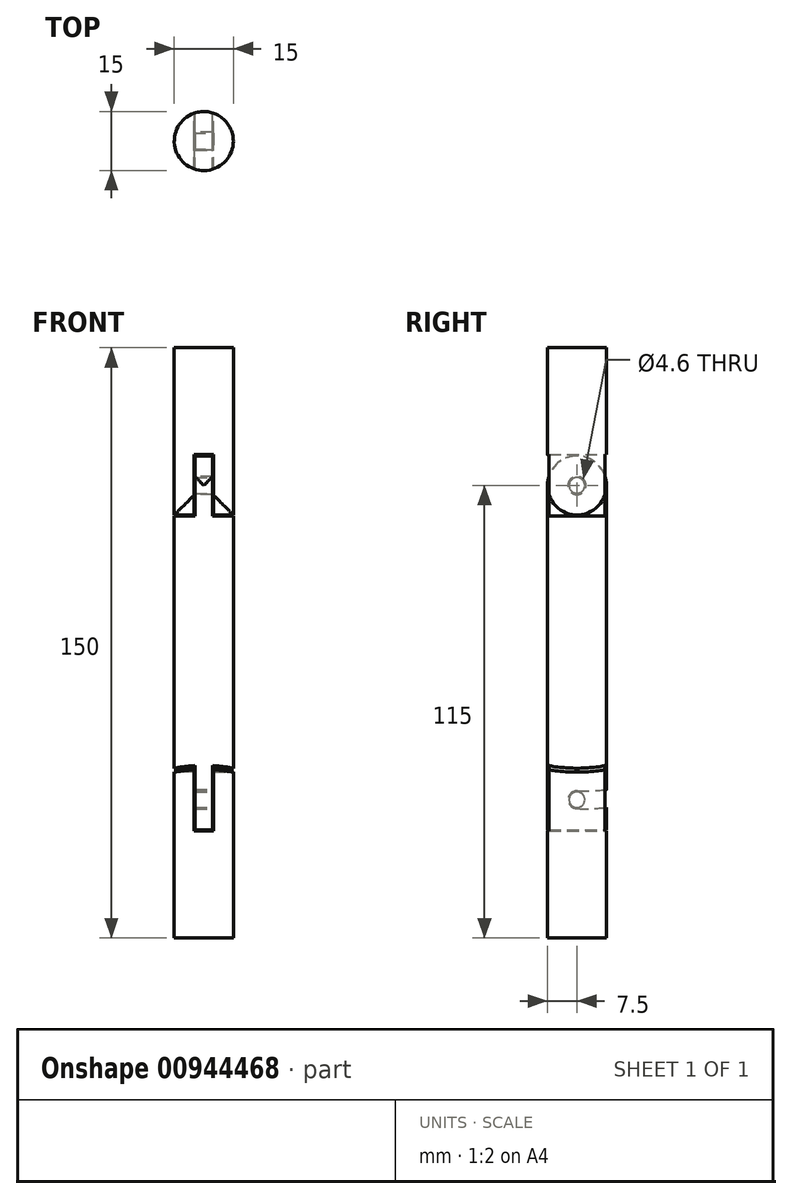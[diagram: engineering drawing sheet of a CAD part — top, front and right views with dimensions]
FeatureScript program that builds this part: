
annotation { "Feature Type Name" : "Feature", "Feature Type Description" : "" }
export const myFeature = defineFeature(function(context is Context, id is Id, definition is map)
    precondition{}
    {
        {
            var Q0;
            Q0=qCreatedBy(makeId("Top.planeOp"),FACE);
            var sketch = newSketch(context, id + "F0", { "sketchPlane" : qUnion([Q0])});
            skCircle(sketch, "E0", {"center": v(0, 0) * mm, "radius": 7.5 * mm});
            skSolve(sketch);
        }
        {
            var Q0;
            Q0 = qSketchRegion(id + "F0", true);
            extrude(context, id + "F1", {"entities" : qUnion([Q0]), "endBound" : BoundingType.SYMMETRIC, "depth" : 150 * mm, "offsetDistance" : 25 * mm});
        }
        {
            var Q0;
            Q0=qCreatedBy(makeId("Front.planeOp"),FACE);
            var sketch = newSketch(context, id + "F2", { "sketchPlane" : qUnion([Q0])});
            skLineSegment(sketch, "E1", {"start": v(0, 0) * mm, "end": v(0, 40) * mm});
            skLineSegment(sketch, "E2", {"start": v(0, 40) * mm, "end": v(2.2, 40) * mm});
            skLineSegment(sketch, "E3", {"start": v(2.2, 40) * mm, "end": v(2.2, 47.5) * mm});
            skLineSegment(sketch, "E4", {"start": v(2.2, 47.5) * mm, "end": v(0, 47.5) * mm});
            skLineSegment(sketch, "E5.MirrorCS", {"start": v(2.2, 40) * mm, "end": v(2.2, 32.5) * mm});
            skLineSegment(sketch, "E6.MirrorCS", {"start": v(2.2, 32.5) * mm, "end": v(0, 32.5) * mm});
            skLineSegment(sketch, "E7.MirrorCS", {"start": v(-2.2, 40) * mm, "end": v(-2.2, 47.5) * mm});
            skLineSegment(sketch, "E8.MirrorCS", {"start": v(-2.2, 47.5) * mm, "end": v(0, 47.5) * mm});
            skLineSegment(sketch, "E9.MirrorCS", {"start": v(-2.2, 32.5) * mm, "end": v(0, 32.5) * mm});
            skLineSegment(sketch, "E10.MirrorCS", {"start": v(-2.2, 40) * mm, "end": v(-2.2, 32.5) * mm});
            skLineSegment(sketch, "E11", {"start": v(0, 47.5) * mm, "end": v(0, 32.5) * mm});
            skLineSegment(sketch, "E12.0", {"start": v(2.5, 40) * mm, "end": v(2.5, 47.8) * mm});
            skLineSegment(sketch, "E12.1", {"start": v(2.5, 40) * mm, "end": v(2.5, 32.2) * mm});
            skLineSegment(sketch, "E12.2", {"start": v(2.5, 47.8) * mm, "end": v(0, 47.8) * mm});
            skLineSegment(sketch, "E12.3", {"start": v(2.5, 32.2) * mm, "end": v(0, 32.2) * mm});
            skLineSegment(sketch, "E12.4", {"start": v(-2.5, 47.8) * mm, "end": v(0, 47.8) * mm});
            skLineSegment(sketch, "E12.5", {"start": v(-2.5, 42.19) * mm, "end": v(-2.5, 47.8) * mm});
            skLineSegment(sketch, "E12.6", {"start": v(-2.5, 42.19) * mm, "end": v(-2.5, 32.2) * mm});
            skLineSegment(sketch, "E12.7", {"start": v(-2.5, 32.2) * mm, "end": v(0, 32.2) * mm});
            skLineSegment(sketch, "E13", {"start": v(2.2, 32.5) * mm, "end": v(2.2, 32.2) * mm});
            skPoint(sketch, "E13.endSnap0", {"position": v(1.25, 32.2) * mm});
            skLineSegment(sketch, "E14", {"start": v(-2.2, 32.5) * mm, "end": v(-2.2, 32.2) * mm});
            skLineSegment(sketch, "E15.MirrorCS", {"start": v(0, 0) * mm, "end": v(0, -40) * mm});
            skLineSegment(sketch, "E16.MirrorCS", {"start": v(2.5, -40) * mm, "end": v(2.5, -47.8) * mm});
            skLineSegment(sketch, "E17.MirrorCS", {"start": v(2.5, -47.8) * mm, "end": v(0, -47.8) * mm});
            skLineSegment(sketch, "E18.MirrorCS", {"start": v(-2.5, -47.8) * mm, "end": v(0, -47.8) * mm});
            skLineSegment(sketch, "E19.MirrorCS", {"start": v(-2.5, -42.19) * mm, "end": v(-2.5, -47.8) * mm});
            skLineSegment(sketch, "E20.MirrorCS", {"start": v(-2.2, -40) * mm, "end": v(-2.2, -47.5) * mm});
            skLineSegment(sketch, "E21.MirrorCS", {"start": v(-2.2, -47.5) * mm, "end": v(0, -47.5) * mm});
            skLineSegment(sketch, "E22.MirrorCS", {"start": v(2.2, -47.5) * mm, "end": v(0, -47.5) * mm});
            skLineSegment(sketch, "E23.MirrorCS", {"start": v(2.2, -40) * mm, "end": v(2.2, -47.5) * mm});
            skLineSegment(sketch, "E24.MirrorCS", {"start": v(-2.5, -42.19) * mm, "end": v(-2.5, -32.2) * mm});
            skLineSegment(sketch, "E25.MirrorCS", {"start": v(-2.2, -40) * mm, "end": v(-2.2, -32.5) * mm});
            skLineSegment(sketch, "E26.MirrorCS", {"start": v(2.2, -40) * mm, "end": v(2.2, -32.5) * mm});
            skLineSegment(sketch, "E27.MirrorCS", {"start": v(2.5, -40) * mm, "end": v(2.5, -32.2) * mm});
            skLineSegment(sketch, "E28.MirrorCS", {"start": v(2.5, -32.2) * mm, "end": v(0, -32.2) * mm});
            skLineSegment(sketch, "E29.MirrorCS", {"start": v(2.2, -32.5) * mm, "end": v(0, -32.5) * mm});
            skLineSegment(sketch, "E30.MirrorCS", {"start": v(-2.2, -32.5) * mm, "end": v(0, -32.5) * mm});
            skLineSegment(sketch, "E31.MirrorCS", {"start": v(-2.5, -32.2) * mm, "end": v(0, -32.2) * mm});
            skLineSegment(sketch, "E32.MirrorCS", {"start": v(2.2, -32.5) * mm, "end": v(2.2, -32.2) * mm});
            skLineSegment(sketch, "E33.MirrorCS", {"start": v(-2.2, -32.5) * mm, "end": v(-2.2, -32.2) * mm});
            skSolve(sketch);
        }
        {
            var Q0;
            Q0=makeQuery(id+"F2.imprint","IMPRINT",FACE,{"disambiguationData":[TD([[makeQuery(id+"F2.imprint","IMPRINT",EDGE,{"derivedFrom":sQuery(id+"F2.wireOp",EDGE,"E3")}),-1.0]])]});
            extrude(context, id + "F3", {"entities" : qUnion([Q0]), "operationType" : NewBodyOperationType.REMOVE, "endBound" : BoundingType.SYMMETRIC, "depth" : 25 * mm, "offsetDistance" : 25 * mm});
        }
        {
            var Q0;
            Q0=makeQuery(id+"F3.boolean.opBoolean","COPY",FACE,{"derivedFrom":makeQuery(id+"F3.opExtrude","SWEPT_FACE",FACE,{"disambiguationData":[OSD([sQuery(id+"F2.wireOp",EDGE,"E3"),sQuery(id+"F2.wireOp",EDGE,"E5.MirrorCS"),sQuery(id+"F2.wireOp",EDGE,"E13")])]})});
            cPlane(context, id + "F4", {"entities" : qUnion([Q0]), "cplaneType" : CPlaneType.OFFSET, "offset" : .15 * mm, "width" : 150 * mm, "height" : 150 * mm});
        }
        {
            var Q0;
            Q0=qCreatedBy(id+"F4.planeOp",FACE);
            var sketch = newSketch(context, id + "F5", { "sketchPlane" : qUnion([Q0])});
            skLineSegment(sketch, "E34", {"start": v(0, 0) * mm, "end": v(0, 40) * mm});
            skCircle(sketch, "E35", {"center": v(0, 40) * mm, "radius": 2 * mm});
            skCircle(sketch, "E36", {"center": v(0, 40) * mm, "radius": 2.3 * mm});
            skCircle(sketch, "E37", {"center": v(0, 40) * mm, "radius": 7.8 * mm});
            skCircle(sketch, "E38", {"center": v(0, 40) * mm, "radius": 7.5 * mm});
            skLineSegment(sketch, "E39", {"start": v(0, 40) * mm, "end": v(-7.5, 40) * mm});
            skLineSegment(sketch, "E40", {"start": v(-7.5, 40) * mm, "end": v(7.8, 40) * mm});
            skLineSegment(sketch, "E41", {"start": v(7.8, 40) * mm, "end": v(7.8, 47.8) * mm});
            skLineSegment(sketch, "E42", {"start": v(7.8, 47.8) * mm, "end": v(0, 47.8) * mm});
            skLineSegment(sketch, "E43.MirrorCS", {"start": v(-7.8, 47.8) * mm, "end": v(0, 47.8) * mm});
            skLineSegment(sketch, "E44.MirrorCS", {"start": v(-7.8, 40) * mm, "end": v(-7.8, 47.8) * mm});
            skLineSegment(sketch, "E45.MirrorCS", {"start": v(7.8, 40) * mm, "end": v(7.8, 32.2) * mm});
            skLineSegment(sketch, "E46.MirrorCS", {"start": v(7.8, 32.2) * mm, "end": v(0, 32.2) * mm});
            skLineSegment(sketch, "E47.MirrorCS", {"start": v(-7.8, 32.2) * mm, "end": v(0, 32.2) * mm});
            skLineSegment(sketch, "E48.MirrorCS", {"start": v(-7.8, 40) * mm, "end": v(-7.8, 32.2) * mm});
            skLineSegment(sketch, "E49", {"start": v(-7.5, 40) * mm, "end": v(-7.8, 40) * mm});
            skSolve(sketch);
        }
        {
            var Q0;
            Q0=makeQuery(id+"F3.boolean.opBoolean","COPY",FACE,{"derivedFrom":makeQuery(id+"F3.opExtrude","SWEPT_FACE",FACE,{"disambiguationData":[OSD([sQuery(id+"F2.wireOp",EDGE,"E7.MirrorCS"),sQuery(id+"F2.wireOp",EDGE,"E10.MirrorCS"),sQuery(id+"F2.wireOp",EDGE,"E14")])]})});
            cPlane(context, id + "F6", {"entities" : qUnion([Q0]), "cplaneType" : CPlaneType.OFFSET, "offset" : .15 * mm, "width" : 150 * mm, "height" : 150 * mm});
        }
        {
            var Q0;
            Q0=qCreatedBy(id+"F6.planeOp",FACE);
            var sketch = newSketch(context, id + "F7", { "sketchPlane" : qUnion([Q0])});
            skLineSegment(sketch, "E50", {"start": v(0, 0) * mm, "end": v(0, 40) * mm});
            skCircle(sketch, "E51", {"center": v(0, 40) * mm, "radius": 2 * mm});
            skCircle(sketch, "E52", {"center": v(0, 40) * mm, "radius": 2.3 * mm});
            skCircle(sketch, "E53", {"center": v(0, 40) * mm, "radius": 7.8 * mm});
            skCircle(sketch, "E54", {"center": v(0, 40) * mm, "radius": 7.5 * mm});
            skLineSegment(sketch, "E55", {"start": v(0, 40) * mm, "end": v(-7.5, 40) * mm});
            skLineSegment(sketch, "E56", {"start": v(-7.5, 40) * mm, "end": v(7.8, 40) * mm});
            skLineSegment(sketch, "E57", {"start": v(7.8, 40) * mm, "end": v(7.8, 47.8) * mm});
            skLineSegment(sketch, "E58", {"start": v(7.8, 47.8) * mm, "end": v(0, 47.8) * mm});
            skLineSegment(sketch, "E59.MirrorCS", {"start": v(-7.8, 47.8) * mm, "end": v(0, 47.8) * mm});
            skLineSegment(sketch, "E60.MirrorCS", {"start": v(-7.8, 40) * mm, "end": v(-7.8, 47.8) * mm});
            skLineSegment(sketch, "E61.MirrorCS", {"start": v(7.8, 40) * mm, "end": v(7.8, 32.2) * mm});
            skLineSegment(sketch, "E62.MirrorCS", {"start": v(7.8, 32.2) * mm, "end": v(0, 32.2) * mm});
            skLineSegment(sketch, "E63.MirrorCS", {"start": v(-7.8, 32.2) * mm, "end": v(0, 32.2) * mm});
            skLineSegment(sketch, "E64.MirrorCS", {"start": v(-7.8, 40) * mm, "end": v(-7.8, 32.2) * mm});
            skLineSegment(sketch, "E65", {"start": v(-7.5, 40) * mm, "end": v(-7.8, 40) * mm});
            skSolve(sketch);
        }
        {
            var Q0;
            {var subQ0=sQuery(id+"F7.wireOp",EDGE,"E55");var subQ1=sQuery(id+"F7.wireOp",EDGE,"E51");var subQ2=makeQuery(id+"F7.imprint","INTERSECT",VERTEX,{"derivedFrom":[subQ1,subQ0]});Q0=makeQuery(id+"F7.imprint","IMPRINT",FACE,{"disambiguationData":[TD([[makeQuery(id+"F7.imprint","IMPRINT",EDGE,{"disambiguationData":[TD([[subQ2,1.0]])],"derivedFrom":subQ1}),1.0]])]});}
            var Q1;
            {var subQ1=sQuery(id+"F7.wireOp",EDGE,"E50");var subQ3=sQuery(id+"F7.wireOp",EDGE,"E51");var subQ4=makeQuery(id+"F7.imprint","INTERSECT",VERTEX,{"derivedFrom":[subQ1,subQ3]});Q1=makeQuery(id+"F7.imprint","IMPRINT",FACE,{"disambiguationData":[TD([[makeQuery(id+"F7.imprint","IMPRINT",EDGE,{"disambiguationData":[TD([[subQ4,-1.0]])],"derivedFrom":subQ3}),1.0]])]});}
            var Q2;
            {var subQ0=sQuery(id+"F7.wireOp",EDGE,"E52");var subQ1=sQuery(id+"F7.wireOp",EDGE,"E50");var subQ2=makeQuery(id+"F7.imprint","INTERSECT",VERTEX,{"derivedFrom":[subQ1,subQ0]});Q2=makeQuery(id+"F7.imprint","IMPRINT",FACE,{"disambiguationData":[TD([[makeQuery(id+"F7.imprint","IMPRINT",EDGE,{"disambiguationData":[TD([[subQ2,-1.0]])],"derivedFrom":subQ1}),-1.0]])]});}
            var Q3;
            {var subQ1=sQuery(id+"F7.wireOp",EDGE,"E50");var subQ3=sQuery(id+"F7.wireOp",EDGE,"E51");var subQ4=makeQuery(id+"F7.imprint","INTERSECT",VERTEX,{"derivedFrom":[subQ1,subQ3]});Q3=makeQuery(id+"F7.imprint","IMPRINT",FACE,{"disambiguationData":[TD([[makeQuery(id+"F7.imprint","IMPRINT",EDGE,{"disambiguationData":[TD([[subQ4,1.0]])],"derivedFrom":subQ3}),1.0]])]});}
            var Q4;
            {var subQ0=sQuery(id+"F7.wireOp",EDGE,"E52");var subQ1=sQuery(id+"F7.wireOp",EDGE,"E50");var subQ2=makeQuery(id+"F7.imprint","INTERSECT",VERTEX,{"derivedFrom":[subQ1,subQ0]});Q4=makeQuery(id+"F7.imprint","IMPRINT",FACE,{"disambiguationData":[TD([[makeQuery(id+"F7.imprint","IMPRINT",EDGE,{"disambiguationData":[TD([[subQ2,-1.0]])],"derivedFrom":subQ1}),1.0]])]});}
            var Q5;
            {var subQ0=sQuery(id+"F7.wireOp",EDGE,"E55");var subQ1=sQuery(id+"F7.wireOp",EDGE,"E51");var subQ2=makeQuery(id+"F7.imprint","INTERSECT",VERTEX,{"derivedFrom":[subQ1,subQ0]});Q5=makeQuery(id+"F7.imprint","IMPRINT",FACE,{"disambiguationData":[TD([[makeQuery(id+"F7.imprint","IMPRINT",EDGE,{"disambiguationData":[TD([[subQ2,1.0]])],"derivedFrom":subQ1}),-1.0]])]});}
            extrude(context, id + "F8", {"entities" : qUnion([Q0, Q1, Q2, Q3, Q4, Q5]), "operationType" : NewBodyOperationType.REMOVE, "oppositeDirection" : true, "depth" : 4.8 * mm, "offsetDistance" : 25 * mm});
        }
        {
            var Q0;
            {var subQ2=sQuery(id+"F5.wireOp",EDGE,"E47.MirrorCS");Q0=makeQuery(id+"F5.imprint","IMPRINT",FACE,{"disambiguationData":[TD([[makeQuery(id+"F5.imprint","IMPRINT",EDGE,{"derivedFrom":subQ2}),1.0]])]});}
            var Q1;
            {var subQ5=sQuery(id+"F5.wireOp",EDGE,"E49");Q1=makeQuery(id+"F5.imprint","IMPRINT",FACE,{"disambiguationData":[TD([[makeQuery(id+"F5.imprint","IMPRINT",EDGE,{"derivedFrom":subQ5}),1.0]])]});}
            var Q2;
            {var subQ0=sQuery(id+"F5.wireOp",EDGE,"E38");var subQ1=sQuery(id+"F5.wireOp",EDGE,"E34");var subQ2=makeQuery(id+"F5.imprint","INTERSECT",VERTEX,{"derivedFrom":[subQ1,subQ0]});Q2=makeQuery(id+"F5.imprint","IMPRINT",FACE,{"disambiguationData":[TD([[makeQuery(id+"F5.imprint","IMPRINT",EDGE,{"disambiguationData":[TD([[subQ2,-1.0]])],"derivedFrom":subQ0}),-1.0]])]});}
            var Q3;
            {var subQ0=sQuery(id+"F5.wireOp",EDGE,"E45.MirrorCS");Q3=makeQuery(id+"F5.imprint","IMPRINT",FACE,{"disambiguationData":[TD([[makeQuery(id+"F5.imprint","IMPRINT",EDGE,{"derivedFrom":subQ0}),-1.0]])]});}
            extrude(context, id + "F9", {"entities" : qUnion([Q0, Q1, Q2, Q3]), "operationType" : NewBodyOperationType.REMOVE, "depth" : 25 * mm, "offsetDistance" : 25 * mm});
        }
        {
            var Q0;
            {var subQ0=sQuery(id+"F5.wireOp",EDGE,"E41");Q0=makeQuery(id+"F5.imprint","IMPRINT",FACE,{"disambiguationData":[TD([[makeQuery(id+"F5.imprint","IMPRINT",EDGE,{"derivedFrom":subQ0}),1.0]])]});}
            var Q1;
            {var subQ0=sQuery(id+"F5.wireOp",EDGE,"E49");Q1=makeQuery(id+"F5.imprint","IMPRINT",FACE,{"disambiguationData":[TD([[makeQuery(id+"F5.imprint","IMPRINT",EDGE,{"derivedFrom":subQ0}),-1.0]])]});}
            var Q2;
            {var subQ0=sQuery(id+"F5.wireOp",EDGE,"E43.MirrorCS");Q2=makeQuery(id+"F5.imprint","IMPRINT",FACE,{"disambiguationData":[TD([[makeQuery(id+"F5.imprint","IMPRINT",EDGE,{"derivedFrom":subQ0}),-1.0]])]});}
            extrude(context, id + "F10", {"entities" : qUnion([Q0, Q1, Q2]), "operationType" : NewBodyOperationType.REMOVE, "oppositeDirection" : true, "depth" : 4.6 * mm, "offsetDistance" : 25 * mm});
        }
        {
            var Q0;
            {var subQ0=sQuery(id+"F7.wireOp",EDGE,"E61.MirrorCS");Q0=makeQuery(id+"F7.imprint","IMPRINT",FACE,{"disambiguationData":[TD([[makeQuery(id+"F7.imprint","IMPRINT",EDGE,{"derivedFrom":subQ0}),-1.0]])]});}
            var Q1;
            {var subQ0=sQuery(id+"F7.wireOp",EDGE,"E54");var subQ1=sQuery(id+"F7.wireOp",EDGE,"E50");var subQ2=makeQuery(id+"F7.imprint","INTERSECT",VERTEX,{"derivedFrom":[subQ1,subQ0]});Q1=makeQuery(id+"F7.imprint","IMPRINT",FACE,{"disambiguationData":[TD([[makeQuery(id+"F7.imprint","IMPRINT",EDGE,{"disambiguationData":[TD([[subQ2,-1.0]])],"derivedFrom":subQ0}),-1.0]])]});}
            var Q2;
            {var subQ5=sQuery(id+"F7.wireOp",EDGE,"E65");Q2=makeQuery(id+"F7.imprint","IMPRINT",FACE,{"disambiguationData":[TD([[makeQuery(id+"F7.imprint","IMPRINT",EDGE,{"derivedFrom":subQ5}),1.0]])]});}
            var Q3;
            {var subQ2=sQuery(id+"F7.wireOp",EDGE,"E63.MirrorCS");Q3=makeQuery(id+"F7.imprint","IMPRINT",FACE,{"disambiguationData":[TD([[makeQuery(id+"F7.imprint","IMPRINT",EDGE,{"derivedFrom":subQ2}),1.0]])]});}
            extrude(context, id + "F11", {"entities" : qUnion([Q0, Q1, Q2, Q3]), "operationType" : NewBodyOperationType.REMOVE, "depth" : 25 * mm, "offsetDistance" : 25 * mm});
        }
        {
            var Q0;
            {var subQ0=sQuery(id+"F7.wireOp",EDGE,"E55");var subQ1=sQuery(id+"F7.wireOp",EDGE,"E51");var subQ2=makeQuery(id+"F7.imprint","INTERSECT",VERTEX,{"derivedFrom":[subQ1,subQ0]});Q0=makeQuery(id+"F7.imprint","IMPRINT",FACE,{"disambiguationData":[TD([[makeQuery(id+"F7.imprint","IMPRINT",EDGE,{"disambiguationData":[TD([[subQ2,1.0]])],"derivedFrom":subQ1}),1.0]])]});}
            var Q1;
            {var subQ1=sQuery(id+"F7.wireOp",EDGE,"E50");var subQ3=sQuery(id+"F7.wireOp",EDGE,"E51");var subQ4=makeQuery(id+"F7.imprint","INTERSECT",VERTEX,{"derivedFrom":[subQ1,subQ3]});Q1=makeQuery(id+"F7.imprint","IMPRINT",FACE,{"disambiguationData":[TD([[makeQuery(id+"F7.imprint","IMPRINT",EDGE,{"disambiguationData":[TD([[subQ4,1.0]])],"derivedFrom":subQ3}),1.0]])]});}
            var Q2;
            {var subQ0=sQuery(id+"F7.wireOp",EDGE,"E52");var subQ1=sQuery(id+"F7.wireOp",EDGE,"E50");var subQ2=makeQuery(id+"F7.imprint","INTERSECT",VERTEX,{"derivedFrom":[subQ1,subQ0]});Q2=makeQuery(id+"F7.imprint","IMPRINT",FACE,{"disambiguationData":[TD([[makeQuery(id+"F7.imprint","IMPRINT",EDGE,{"disambiguationData":[TD([[subQ2,-1.0]])],"derivedFrom":subQ1}),-1.0]])]});}
            var Q3;
            {var subQ1=sQuery(id+"F7.wireOp",EDGE,"E50");var subQ3=sQuery(id+"F7.wireOp",EDGE,"E51");var subQ4=makeQuery(id+"F7.imprint","INTERSECT",VERTEX,{"derivedFrom":[subQ1,subQ3]});Q3=makeQuery(id+"F7.imprint","IMPRINT",FACE,{"disambiguationData":[TD([[makeQuery(id+"F7.imprint","IMPRINT",EDGE,{"disambiguationData":[TD([[subQ4,-1.0]])],"derivedFrom":subQ3}),1.0]])]});}
            var Q4;
            {var subQ0=sQuery(id+"F7.wireOp",EDGE,"E55");var subQ1=sQuery(id+"F7.wireOp",EDGE,"E51");var subQ2=makeQuery(id+"F7.imprint","INTERSECT",VERTEX,{"derivedFrom":[subQ1,subQ0]});Q4=makeQuery(id+"F7.imprint","IMPRINT",FACE,{"disambiguationData":[TD([[makeQuery(id+"F7.imprint","IMPRINT",EDGE,{"disambiguationData":[TD([[subQ2,1.0]])],"derivedFrom":subQ1}),-1.0]])]});}
            var Q5;
            {var subQ0=sQuery(id+"F7.wireOp",EDGE,"E52");var subQ1=sQuery(id+"F7.wireOp",EDGE,"E50");var subQ2=makeQuery(id+"F7.imprint","INTERSECT",VERTEX,{"derivedFrom":[subQ1,subQ0]});Q5=makeQuery(id+"F7.imprint","IMPRINT",FACE,{"disambiguationData":[TD([[makeQuery(id+"F7.imprint","IMPRINT",EDGE,{"disambiguationData":[TD([[subQ2,-1.0]])],"derivedFrom":subQ1}),1.0]])]});}
            extrude(context, id + "F12", {"entities" : qUnion([Q0, Q1, Q2, Q3, Q4, Q5]), "operationType" : NewBodyOperationType.REMOVE, "oppositeDirection" : true, "depth" : 4.7 * mm, "offsetDistance" : 25 * mm});
        }
        {
            var Q0;
            {var subQ0=sQuery(id+"F7.wireOp",EDGE,"E55");var subQ1=sQuery(id+"F7.wireOp",EDGE,"E51");var subQ2=makeQuery(id+"F7.imprint","INTERSECT",VERTEX,{"derivedFrom":[subQ1,subQ0]});Q0=makeQuery(id+"F7.imprint","IMPRINT",FACE,{"disambiguationData":[TD([[makeQuery(id+"F7.imprint","IMPRINT",EDGE,{"disambiguationData":[TD([[subQ2,1.0]])],"derivedFrom":subQ1}),1.0]])]});}
            var Q1;
            {var subQ1=sQuery(id+"F7.wireOp",EDGE,"E50");var subQ3=sQuery(id+"F7.wireOp",EDGE,"E51");var subQ4=makeQuery(id+"F7.imprint","INTERSECT",VERTEX,{"derivedFrom":[subQ1,subQ3]});Q1=makeQuery(id+"F7.imprint","IMPRINT",FACE,{"disambiguationData":[TD([[makeQuery(id+"F7.imprint","IMPRINT",EDGE,{"disambiguationData":[TD([[subQ4,1.0]])],"derivedFrom":subQ3}),1.0]])]});}
            var Q2;
            {var subQ1=sQuery(id+"F7.wireOp",EDGE,"E50");var subQ3=sQuery(id+"F7.wireOp",EDGE,"E51");var subQ4=makeQuery(id+"F7.imprint","INTERSECT",VERTEX,{"derivedFrom":[subQ1,subQ3]});Q2=makeQuery(id+"F7.imprint","IMPRINT",FACE,{"disambiguationData":[TD([[makeQuery(id+"F7.imprint","IMPRINT",EDGE,{"disambiguationData":[TD([[subQ4,-1.0]])],"derivedFrom":subQ3}),1.0]])]});}
            extrude(context, id + "F13", {"entities" : qUnion([Q0, Q1, Q2]), "operationType" : NewBodyOperationType.ADD, "depth" : 3 * mm, "offsetDistance" : 25 * mm, "hasSecondDirection" : true, "secondDirectionOppositeDirection" : true, "secondDirectionDepth" : 6 * mm});
        }
        {
            var Q0;
            Q0=makeQuery(id+"F2.imprint","IMPRINT",FACE,{"disambiguationData":[TD([[makeQuery(id+"F2.imprint","IMPRINT",EDGE,{"derivedFrom":sQuery(id+"F2.wireOp",EDGE,"E16.MirrorCS")}),-1.0]])]});
            extrude(context, id + "F14", {"entities" : qUnion([Q0]), "operationType" : NewBodyOperationType.REMOVE, "endBound" : BoundingType.SYMMETRIC, "depth" : 25 * mm, "offsetDistance" : 25 * mm});
        }
        {
            var Q0;
            Q0=makeQuery(id+"F14.boolean.opBoolean","COPY",FACE,{"derivedFrom":makeQuery(id+"F14.opExtrude","SWEPT_FACE",FACE,{"disambiguationData":[OSD([sQuery(id+"F2.wireOp",EDGE,"E23.MirrorCS"),sQuery(id+"F2.wireOp",EDGE,"E26.MirrorCS"),sQuery(id+"F2.wireOp",EDGE,"E32.MirrorCS")])]})});
            var sketch = newSketch(context, id + "F15", { "sketchPlane" : qUnion([Q0])});
            skLineSegment(sketch, "E66", {"start": v(-7.17, -32.2) * mm, "end": v(0, -39.85) * mm});
            skLineSegment(sketch, "E67", {"start": v(7.17, -32.2) * mm, "end": v(0, -39.85) * mm});
            skLineSegment(sketch, "E68", {"start": v(0, -39.85) * mm, "end": v(7.17, -47.5) * mm});
            skLineSegment(sketch, "E69", {"start": v(0, -39.85) * mm, "end": v(-7.17, -47.5) * mm});
            skArc(sketch, "E70", {"start": v(0, -39.85) * mm, "mid": v(6.9, -39.59) * mm, "end": v(13.66, -38.14) * mm});
            skArc(sketch, "E71.0.startCap", {"start": v(-0.11, -42.1) * mm, "mid": v(-2.25, -39.74) * mm, "end": v(0.11, -37.6) * mm});
            skArc(sketch, "E71.0.endCap", {"start": v(13, -35.99) * mm, "mid": v(15.81, -37.48) * mm, "end": v(14.32, -40.29) * mm});
            skArc(sketch, "E71.0.left", {"start": v(0.11, -37.6) * mm, "mid": v(6.63, -37.36) * mm, "end": v(13, -35.99) * mm});
            skArc(sketch, "E71.0.right", {"start": v(-0.11, -42.1) * mm, "mid": v(7.19, -41.82) * mm, "end": v(14.32, -40.29) * mm});
            skCircle(sketch, "E72", {"center": v(0, -39.85) * mm, "radius": 2 * mm});
            skSolve(sketch);
        }
        {
            var Q0;
            Q0 = qSketchRegion(id + "F15", true);
            extrude(context, id + "F16", {"entities" : qUnion([Q0]), "operationType" : NewBodyOperationType.REMOVE, "oppositeDirection" : true, "depth" : 4.6 * mm, "offsetDistance" : 25 * mm});
        }
        {
            var Q0;
            Q0=qCreatedBy(makeId("Right.planeOp"),FACE);
            cPlane(context, id + "F17", {"entities" : qUnion([Q0]), "cplaneType" : CPlaneType.OFFSET, "offset" : 10 * mm, "oppositeDirection" : true, "width" : 150 * mm, "height" : 150 * mm});
        }
        {
            var Q0;
            Q0=qCreatedBy(makeId("Right.planeOp"),FACE);
            cPlane(context, id + "F18", {"entities" : qUnion([Q0]), "cplaneType" : CPlaneType.OFFSET, "offset" : 10 * mm, "width" : 150 * mm, "height" : 150 * mm});
        }
        {
            var Q0;
            Q0=qCreatedBy(id+"F18.planeOp",FACE);
            var sketch = newSketch(context, id + "F19", { "sketchPlane" : qUnion([Q0])});
            skCircle(sketch, "E73", {"center": v(0, 8) * mm, "radius": 39.85 * mm});
            skCircle(sketch, "E74", {"center": v(0, 8) * mm, "radius": 40.85 * mm});
            skLineSegment(sketch, "E75", {"start": v(0, -32.84) * mm, "end": v(9.2, -32.84) * mm});
            skPoint(sketch, "E76.start.orphan", {"position": v(0, -31.84) * mm});
            skLineSegment(sketch, "E77", {"start": v(10.2, -30.52) * mm, "end": v(10.2, -31.55) * mm});
            skLineSegment(sketch, "E78", {"start": v(-10.4, -30.46) * mm, "end": v(-10.4, -31.5) * mm});
            skLineSegment(sketch, "E79", {"start": v(0, 8) * mm, "end": v(0, 0) * mm});
            skSolve(sketch);
        }
        {
            var Q0;
            {var subQ2=sQuery(id+"F19.wireOp",EDGE,"E77");Q0=makeQuery(id+"F19.imprint","IMPRINT",FACE,{"disambiguationData":[TD([[makeQuery(id+"F19.imprint","IMPRINT",EDGE,{"derivedFrom":subQ2}),-1.0]])]});}
            extrude(context, id + "F20", {"entities" : qUnion([Q0]), "operationType" : NewBodyOperationType.REMOVE, "oppositeDirection" : true, "depth" : 7.8 * mm, "offsetDistance" : 25 * mm});
        }
        {
            var Q0;
            Q0=qCreatedBy(id+"F17.planeOp",FACE);
            cPlane(context, id + "F21", {"entities" : qUnion([Q0]), "cplaneType" : CPlaneType.OFFSET, "offset" : 6 * mm, "oppositeDirection" : true, "width" : 150 * mm, "height" : 150 * mm});
        }
        {
            var Q0;
            Q0=qCreatedBy(id+"F21.planeOp",FACE);
            var sketch = newSketch(context, id + "F22", { "sketchPlane" : qUnion([Q0])});
            skCircle(sketch, "E80", {"center": v(0, 8) * mm, "radius": 39.85 * mm});
            skCircle(sketch, "E81", {"center": v(0, 8) * mm, "radius": 40.85 * mm});
            skLineSegment(sketch, "E82", {"start": v(0, -32.84) * mm, "end": v(9.2, -32.84) * mm});
            skPoint(sketch, "E83.start.orphan", {"position": v(0, -31.84) * mm});
            skLineSegment(sketch, "E84", {"start": v(10.2, -30.52) * mm, "end": v(10.2, -31.55) * mm});
            skLineSegment(sketch, "E85", {"start": v(-10.4, -30.46) * mm, "end": v(-10.4, -31.5) * mm});
            skLineSegment(sketch, "E86", {"start": v(0, 8) * mm, "end": v(0, 0) * mm});
            skSolve(sketch);
        }
        {
            var Q0;
            {var subQ2=sQuery(id+"F22.wireOp",EDGE,"E84");Q0=makeQuery(id+"F22.imprint","IMPRINT",FACE,{"disambiguationData":[TD([[makeQuery(id+"F22.imprint","IMPRINT",EDGE,{"derivedFrom":subQ2}),-1.0]])]});}
            extrude(context, id + "F23", {"entities" : qUnion([Q0]), "operationType" : NewBodyOperationType.REMOVE, "depth" : 13.8 * mm, "offsetDistance" : 25 * mm});
        }
        {
            var Q0;
            Q0=makeQuery(id+"F16.boolean.opBoolean","SPLIT",FACE,{"disambiguationData":[TD([makeQuery(id+"F16.opExtrude","SWEPT_FACE",FACE,{"disambiguationData":[OSD([sQuery(id+"F15.wireOp",EDGE,"E72")])]})])],"derivedFrom":makeQuery(id+"F14.boolean.opBoolean","COPY",FACE,{"derivedFrom":makeQuery(id+"F14.opExtrude","SWEPT_FACE",FACE,{"disambiguationData":[OSD([sQuery(id+"F2.wireOp",EDGE,"E23.MirrorCS"),sQuery(id+"F2.wireOp",EDGE,"E26.MirrorCS"),sQuery(id+"F2.wireOp",EDGE,"E32.MirrorCS")])]})})});
            var Q1;
            Q1=makeQuery(id+"F16.boolean.opBoolean","SPLIT",FACE,{"disambiguationData":[TD([makeQuery(id+"F16.opExtrude","SWEPT_FACE",FACE,{"disambiguationData":[OSD([sQuery(id+"F15.wireOp",EDGE,"E72")])]})])],"derivedFrom":makeQuery(id+"F14.boolean.opBoolean","COPY",FACE,{"derivedFrom":makeQuery(id+"F14.opExtrude","SWEPT_FACE",FACE,{"disambiguationData":[OSD([sQuery(id+"F2.wireOp",EDGE,"E20.MirrorCS"),sQuery(id+"F2.wireOp",EDGE,"E25.MirrorCS"),sQuery(id+"F2.wireOp",EDGE,"E33.MirrorCS")])]})})});
            extrude(context, id + "F24", {"entities" : qUnion([Q0, Q1]), "operationType" : NewBodyOperationType.ADD, "endBound" : BoundingType.SYMMETRIC, "depth" : 2 * mm, "offsetDistance" : 25 * mm});
        }
    });
